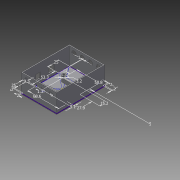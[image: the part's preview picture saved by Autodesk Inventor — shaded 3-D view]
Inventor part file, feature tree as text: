
AUTODESK INVENTOR PART (.ipt)
format: ipt  version: 2013 (Build 170138000, 138)  size: 199,168 bytes
history: native  units: mm
features: extrude x6, sketch x5, projected_geometry x1
ambient origin geometry x8: Origin, YZ Plane, XZ Plane, XY Plane, X Axis, Y Axis, Z Axis, Center Point
bodies: Solid1 (feature_tree)
feature tree (12):
  sketch  "Sketch1"  dims[d0=53.3mm d2=68.6mm]
  extrude  "Extrusion1"  Depth=68.6mm
  extrude  "Extrusion2"  Depth=2.5mm
  extrude  "Extrusion3"  Depth=27.9mm
  extrude  "Extrusion6"  Depth=3.2mm
  extrude  "Extrusion7"  Depth=1.0mm
  extrude  "Extrusion4"  Depth=2.0mm
  sketch  "Sketch2"  dims[d3=14.0mm d4=2.5mm]
  sketch  "Sketch4"  dims[d5=50.8mm d6=27.9mm]
  sketch  "Sketch6"  dims[d7=5.1mm d8=3.2mm]
  sketch  "Sketch7"  dims[d9=25.0mm d10=1.0mm d11=2.0mm d12=2.0mm d13=2.0mm d14=0.0mm d15=40.0mm d16=0.0mm d17=8.3mm d19=4.3mm d20=5.0mm d21=0.0mm d22=13.0mm d24=12.0mm d26=9.0mm d27=12.0mm d28=10.0mm d31=3.25mm d32=5.0mm d33=0.0mm d46=9.9mm d54=12.3mm d56=32.0mm d59=5.0mm d62=25.0mm d63=2.0mm d64=2.0mm d65=3.89mm d66=40.0mm d68=18.0mm d69=10.0mm d71=10.0mm d73=12.3mm d74=0.0mm d75=0.0mm d79=4.0mm d80=20.0mm d81=6.0mm d82=6.0mm d83=20.0mm d84=8.0mm d85=0.0mm d86=10.0mm d87=0.0mm d88=1.5mm d90=1.5mm d92=15.2mm d94=1.3mm]
  projected_geometry  "Projected Loop1"
